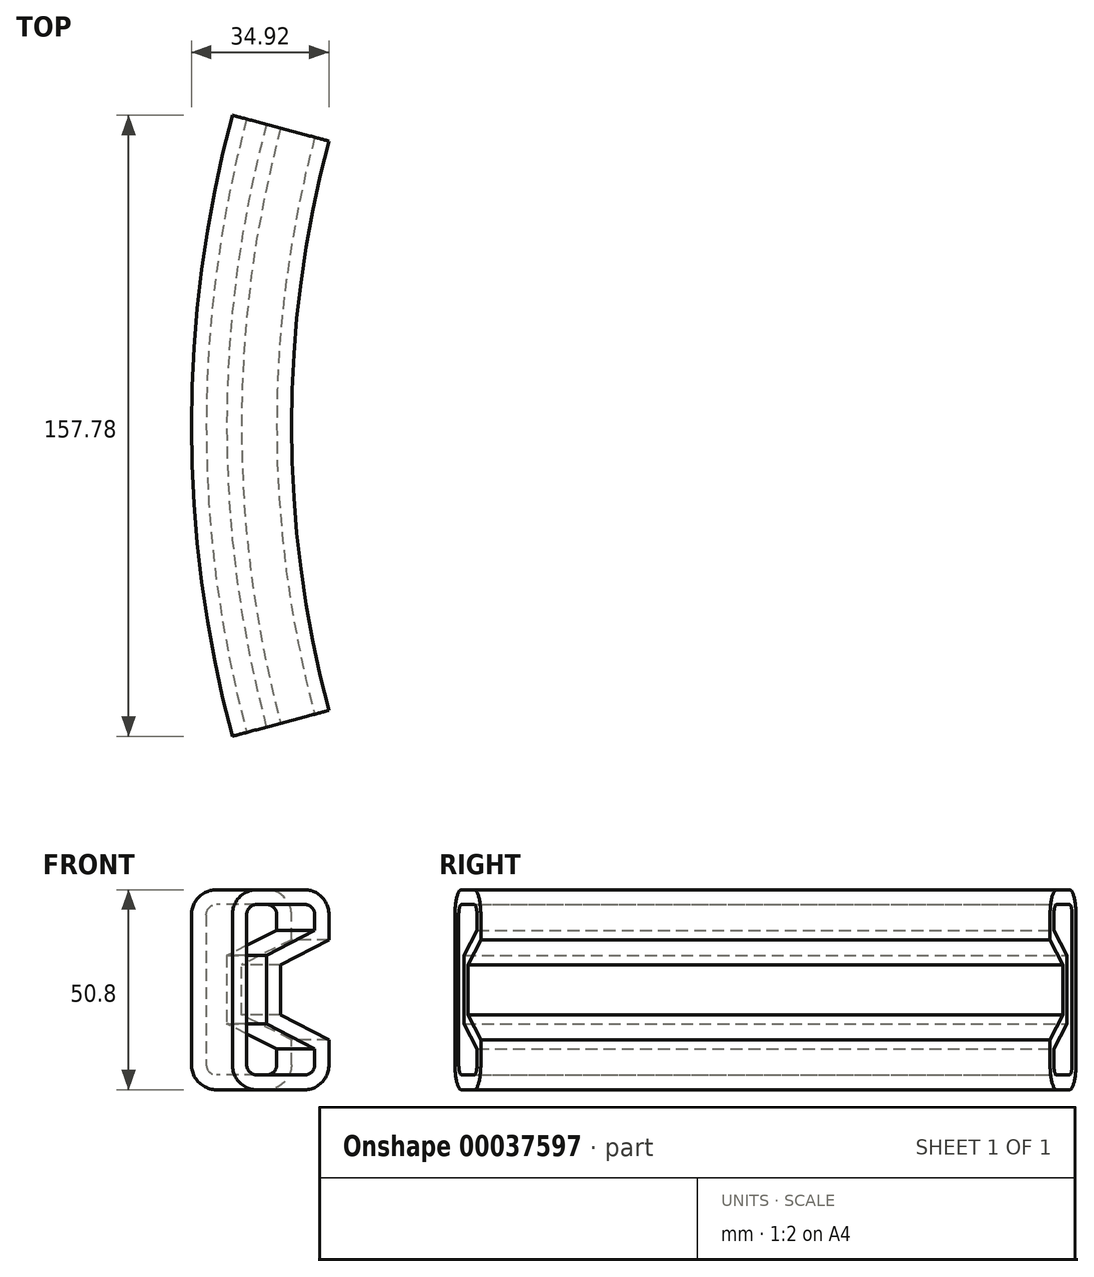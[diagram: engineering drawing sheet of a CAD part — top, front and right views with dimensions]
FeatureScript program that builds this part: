
annotation { "Feature Type Name" : "Feature", "Feature Type Description" : "" }
export const myFeature = defineFeature(function(context is Context, id is Id, definition is map)
    precondition{}
    {
        {
            var Q0;
            Q0=qCreatedBy(makeId("Front.planeOp"),FACE);
            var sketch = newSketch(context, id + "F0", { "sketchPlane" : qUnion([Q0])});
            skLineSegment(sketch, "E0", {"start": v(-49.15, 37.06) * mm, "end": v(-36.45, 37.06) * mm});
            skLineSegment(sketch, "E1", {"start": v(-42.8, 18) * mm, "end": v(-42.8, 5.3) * mm});
            skLineSegment(sketch, "E2", {"start": v(-55.5, 30.7) * mm, "end": v(-55.5, -7.4) * mm});
            skLineSegment(sketch, "E3", {"start": v(-49.15, -13.74) * mm, "end": v(-36.45, -13.74) * mm});
            skPoint(sketch, "E4.visualSharp", {"position": v(-55.5, 37.06) * mm});
            skArc(sketch, "E4.filletArc", {"start": v(-49.15, 37.06) * mm, "mid": v(-53.64, 35.2) * mm, "end": v(-55.5, 30.7) * mm});
            skPoint(sketch, "E5.visualSharp", {"position": v(-55.5, -13.74) * mm});
            skArc(sketch, "E5.filletArc", {"start": v(-55.5, -7.4) * mm, "mid": v(-53.64, -11.88) * mm, "end": v(-49.15, -13.74) * mm});
            skPoint(sketch, "E6.visualSharp", {"position": v(-4.7, -13.74) * mm});
            skArc(sketch, "E6.filletArc", {"start": v(-36.45, -13.74) * mm, "mid": v(-31.96, -11.88) * mm, "end": v(-30.1, -7.4) * mm});
            skPoint(sketch, "E7.visualSharp", {"position": v(-4.7, 37.06) * mm});
            skArc(sketch, "E7.filletArc", {"start": v(-30.1, 30.7) * mm, "mid": v(-31.96, 35.2) * mm, "end": v(-36.45, 37.06) * mm});
            skPoint(sketch, "E8", {"position": v(249.3, 11.66) * mm});
            skLineSegment(sketch, "E9", {"start": v(249.3, 11.66) * mm, "end": v(249.3, 0) * mm});
            skLineSegment(sketch, "E10", {"start": v(-30.1, 24.36) * mm, "end": v(-42.8, 18) * mm});
            skLineSegment(sketch, "E11", {"start": v(-30.1, 24.36) * mm, "end": v(-30.1, 30.7) * mm});
            skLineSegment(sketch, "E12", {"start": v(-30.1, -1.04) * mm, "end": v(-42.8, 5.3) * mm});
            skLineSegment(sketch, "E13", {"start": v(-30.1, -1.04) * mm, "end": v(-30.1, -7.4) * mm});
            skSolve(sketch);
        }
        {
            var Q0;
            Q0=makeQuery(id+"F0.imprint","IMPRINT",FACE,{"disambiguationData":[TD([[makeQuery(id+"F0.imprint","IMPRINT",EDGE,{"derivedFrom":sQuery(id+"F0.wireOp",EDGE,"E0")}),-1.0]])]});
            var Q1;
            Q1=sQuery(id+"F0.wireOp",EDGE,"E0");
            var Q2;
            Q2=sQuery(id+"F0.wireOp",EDGE,"E4.filletArc");
            var Q3;
            Q3=sQuery(id+"F0.wireOp",EDGE,"E2");
            var Q4;
            Q4=sQuery(id+"F0.wireOp",EDGE,"E7.filletArc");
            var Q5;
            Q5=sQuery(id+"F0.wireOp",EDGE,"3352df40-99eb-4d6d-ab64-4eb77467014a");
            var Q6;
            Q6=sQuery(id+"F0.wireOp",EDGE,"e21ff906-9fa8-430d-814f-205eb433ba27");
            var Q7;
            Q7=sQuery(id+"F0.wireOp",EDGE,"E1");
            var Q8;
            Q8=sQuery(id+"F0.wireOp",EDGE,"1820fb43-8a43-468b-8f48-1f127378ad0f");
            var Q9;
            Q9=sQuery(id+"F0.wireOp",EDGE,"9c30f464-c7be-41d6-a98d-f67b8ec0e6ef");
            var Q10;
            Q10=sQuery(id+"F0.wireOp",EDGE,"E6.filletArc");
            var Q11;
            Q11=sQuery(id+"F0.wireOp",EDGE,"E3");
            var Q12;
            Q12=sQuery(id+"F0.wireOp",EDGE,"E5.filletArc");
            var Q13;
            Q13=sQuery(id+"F0.wireOp",EDGE,"E9");
            revolve(context, id + "F1", {"entities" : qUnion([Q0]), "surfaceEntities" : qUnion([Q1, Q2, Q3, Q4, Q5, Q6, Q7, Q8, Q9, Q10, Q11, Q12]), "axis" : qUnion([Q13]), "revolveType" : RevolveType.SYMMETRIC, "angle" : 30 * degree});
        }
        {
            var Q0;
            Q0=makeQuery(id+"F1.opRevolve","CAP_FACE",FACE,{"disambiguationData":[OSD([sQuery(id+"F0.wireOp",EDGE,"E0"),sQuery(id+"F0.wireOp",EDGE,"E1"),sQuery(id+"F0.wireOp",EDGE,"E2"),sQuery(id+"F0.wireOp",EDGE,"E3"),sQuery(id+"F0.wireOp",EDGE,"E4.filletArc"),sQuery(id+"F0.wireOp",EDGE,"E5.filletArc"),sQuery(id+"F0.wireOp",EDGE,"E6.filletArc"),sQuery(id+"F0.wireOp",EDGE,"E7.filletArc"),sQuery(id+"F0.wireOp",EDGE,"E10"),sQuery(id+"F0.wireOp",EDGE,"E11"),sQuery(id+"F0.wireOp",EDGE,"E12"),sQuery(id+"F0.wireOp",EDGE,"E13")])],"isStart":true});
            var sketch = newSketch(context, id + "F2", { "sketchPlane" : qUnion([Q0])});
            skLineSegment(sketch, "E14", {"start": v(240.8, 11.66) * mm, "end": v(240.8, 23.62) * mm});
            skArc(sketch, "E15.0", {"start": v(-42.4, 30.7) * mm, "mid": v(-43.15, 32.5) * mm, "end": v(-44.94, 33.24) * mm});
            skLineSegment(sketch, "E15.1", {"start": v(-57.64, -9.93) * mm, "end": v(-44.94, -9.93) * mm});
            skArc(sketch, "E15.2", {"start": v(-60.18, -7.4) * mm, "mid": v(-59.43, -9.19) * mm, "end": v(-57.64, -9.93) * mm});
            skLineSegment(sketch, "E15.3", {"start": v(-60.18, 30.7) * mm, "end": v(-60.18, -7.4) * mm});
            skArc(sketch, "E15.4", {"start": v(-57.64, 33.24) * mm, "mid": v(-59.43, 32.5) * mm, "end": v(-60.18, 30.7) * mm});
            skArc(sketch, "E15.5", {"start": v(-44.94, -9.93) * mm, "mid": v(-43.15, -9.19) * mm, "end": v(-42.4, -7.4) * mm});
            skLineSegment(sketch, "E15.6", {"start": v(-44.94, 33.24) * mm, "end": v(-57.64, 33.24) * mm});
            skLineSegment(sketch, "E15.7", {"start": v(-42.4, -7.4) * mm, "end": v(-42.4, -3.4) * mm});
            skLineSegment(sketch, "E15.8", {"start": v(-42.4, -3.4) * mm, "end": v(-55.1, 2.95) * mm});
            skLineSegment(sketch, "E15.9", {"start": v(-55.1, 2.95) * mm, "end": v(-55.1, 20.36) * mm});
            skLineSegment(sketch, "E15.10", {"start": v(-55.1, 20.36) * mm, "end": v(-42.4, 26.71) * mm});
            skLineSegment(sketch, "E15.11", {"start": v(-42.4, 26.71) * mm, "end": v(-42.4, 30.7) * mm});
            skSolve(sketch);
        }
        {
            var Q0;
            Q0=makeQuery(id+"F2.imprint","IMPRINT",FACE,{"disambiguationData":[TD([[makeQuery(id+"F2.imprint","IMPRINT",EDGE,{"derivedFrom":sQuery(id+"F2.wireOp",EDGE,"E15.0")}),1.0]])]});
            var Q1;
            Q1=sQuery(id+"F2.wireOp",EDGE,"E14");
            revolve(context, id + "F3", {"operationType" : NewBodyOperationType.ADD, "entities" : qUnion([Q0]), "axis" : qUnion([Q1]), "revolveType" : RevolveType.ONE_DIRECTION, "angle" : 3 * degree});
        }
        {
            var Q0;
            Q0=makeQuery(id+"F1.opRevolve","CAP_FACE",FACE,{"disambiguationData":[OSD([sQuery(id+"F0.wireOp",EDGE,"E0"),sQuery(id+"F0.wireOp",EDGE,"E1"),sQuery(id+"F0.wireOp",EDGE,"E2"),sQuery(id+"F0.wireOp",EDGE,"E3"),sQuery(id+"F0.wireOp",EDGE,"E4.filletArc"),sQuery(id+"F0.wireOp",EDGE,"E5.filletArc"),sQuery(id+"F0.wireOp",EDGE,"E6.filletArc"),sQuery(id+"F0.wireOp",EDGE,"E7.filletArc"),sQuery(id+"F0.wireOp",EDGE,"E10"),sQuery(id+"F0.wireOp",EDGE,"E11"),sQuery(id+"F0.wireOp",EDGE,"E12"),sQuery(id+"F0.wireOp",EDGE,"E13")])],"isStart":false});
            var sketch = newSketch(context, id + "F4", { "sketchPlane" : qUnion([Q0])});
            skLineSegment(sketch, "E16", {"start": v(-240.8, 11.66) * mm, "end": v(-240.8, 25.4) * mm});
            skArc(sketch, "E17.0", {"start": v(60.24, 30.7) * mm, "mid": v(59.48, 32.54) * mm, "end": v(57.64, 33.3) * mm});
            skLineSegment(sketch, "E17.1", {"start": v(55.04, 20.33) * mm, "end": v(55.04, 2.99) * mm});
            skLineSegment(sketch, "E17.2", {"start": v(42.34, 26.68) * mm, "end": v(55.04, 20.33) * mm});
            skLineSegment(sketch, "E17.3", {"start": v(42.34, 30.7) * mm, "end": v(42.34, 26.68) * mm});
            skArc(sketch, "E17.4", {"start": v(44.94, 33.3) * mm, "mid": v(43.1, 32.54) * mm, "end": v(42.34, 30.7) * mm});
            skLineSegment(sketch, "E17.5", {"start": v(55.04, 2.99) * mm, "end": v(42.34, -3.36) * mm});
            skLineSegment(sketch, "E17.6", {"start": v(57.64, 33.3) * mm, "end": v(44.94, 33.3) * mm});
            skLineSegment(sketch, "E17.7", {"start": v(42.34, -3.36) * mm, "end": v(42.34, -7.4) * mm});
            skArc(sketch, "E17.8", {"start": v(42.34, -7.4) * mm, "mid": v(43.1, -9.23) * mm, "end": v(44.94, -9.99) * mm});
            skLineSegment(sketch, "E17.9", {"start": v(44.94, -9.99) * mm, "end": v(57.64, -9.99) * mm});
            skArc(sketch, "E17.10", {"start": v(57.64, -9.99) * mm, "mid": v(59.48, -9.23) * mm, "end": v(60.24, -7.4) * mm});
            skLineSegment(sketch, "E17.11", {"start": v(60.24, -7.4) * mm, "end": v(60.24, 30.7) * mm});
            skSolve(sketch);
        }
        {
            var Q0;
            Q0=makeQuery(id+"F4.imprint","IMPRINT",FACE,{"disambiguationData":[TD([[makeQuery(id+"F4.imprint","IMPRINT",EDGE,{"derivedFrom":sQuery(id+"F4.wireOp",EDGE,"E17.0")}),1.0]])]});
            var Q1;
            Q1=sQuery(id+"F4.wireOp",EDGE,"E16");
            revolve(context, id + "F5", {"operationType" : NewBodyOperationType.REMOVE, "entities" : qUnion([Q0]), "axis" : qUnion([Q1]), "revolveType" : RevolveType.FULL});
        }
    });
